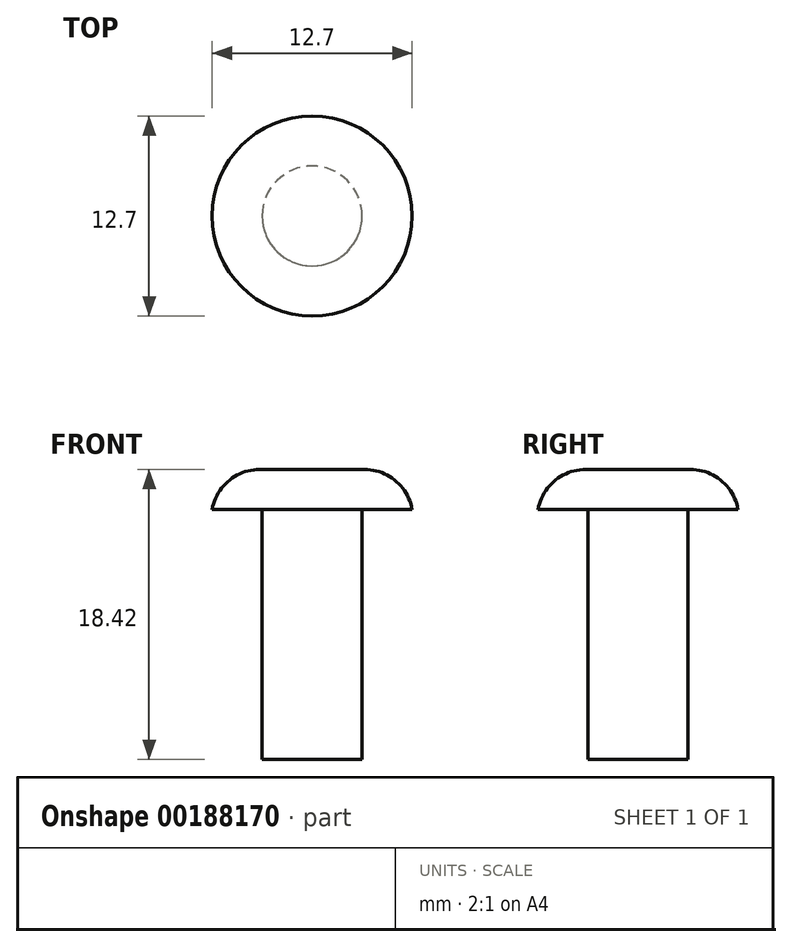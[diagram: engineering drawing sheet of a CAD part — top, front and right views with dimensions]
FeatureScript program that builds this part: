
annotation { "Feature Type Name" : "Feature", "Feature Type Description" : "" }
export const myFeature = defineFeature(function(context is Context, id is Id, definition is map)
    precondition{}
    {
        {
            var Q0;
            Q0=qCreatedBy(makeId("Top.planeOp"),FACE);
            var sketch = newSketch(context, id + "F0", { "sketchPlane" : qUnion([Q0])});
            skCircle(sketch, "E0", {"center": v(0, 0) * mm, "radius": 6.35 * mm});
            skSolve(sketch);
        }
        {
            var Q0;
            Q0=qSketchRegion(id+"F0",true);
            extrude(context, id + "F1", {"entities" : qUnion([Q0]), "depth" : 2.54 * mm});
        }
        {
            var Q0;
            Q0=makeQuery(id+"F1.opExtrude","CAP_EDGE",EDGE,{"disambiguationData":[OSD([sQuery(id+"F0.wireOp",EDGE,"E0")])],"isStart":false});
            fillet(context, id + "F2", {"entities" : qUnion([Q0]), "radius" : 3.07 * mm, "tangentPropagation" : true, "allowEdgeOverflow" : false});
        }
        {
            var Q0;
            Q0=makeQuery(id+"F1.opExtrude","CAP_FACE",FACE,{"disambiguationData":[OSD([sQuery(id+"F0.wireOp",EDGE,"E0")])],"isStart":true});
            var sketch = newSketch(context, id + "F3", { "sketchPlane" : qUnion([Q0])});
            skCircle(sketch, "E1", {"center": v(0, 0) * mm, "radius": 3.18 * mm});
            skSolve(sketch);
        }
        {
            var Q0;
            Q0=qSketchRegion(id+"F3",true);
            extrude(context, id + "F4", {"entities" : qUnion([Q0]), "operationType" : NewBodyOperationType.ADD, "depth" : 15.88 * mm});
        }
    });
